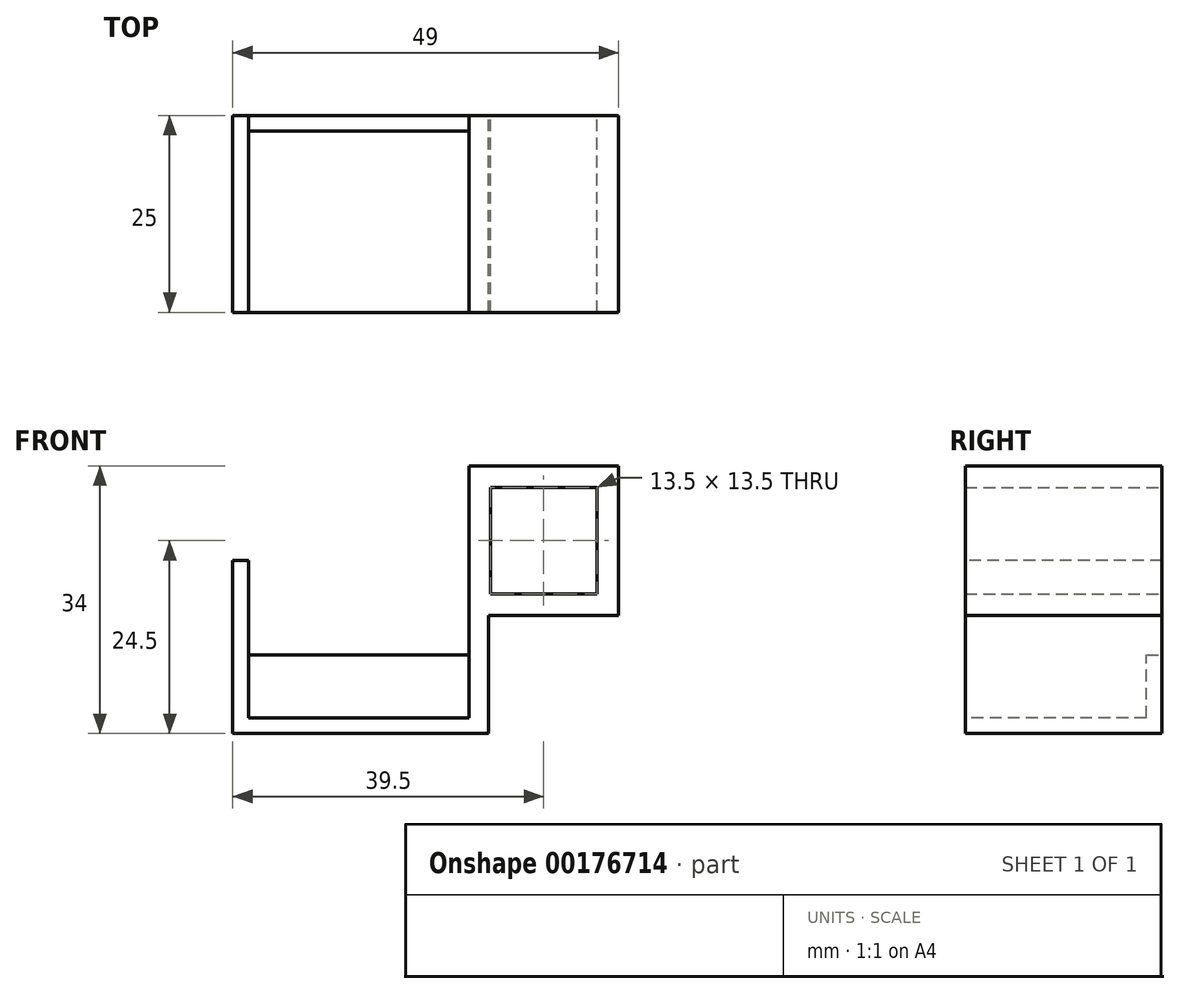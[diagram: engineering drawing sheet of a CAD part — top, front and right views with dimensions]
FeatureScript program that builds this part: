
annotation { "Feature Type Name" : "Feature", "Feature Type Description" : "" }
export const myFeature = defineFeature(function(context is Context, id is Id, definition is map)
    precondition{}
    {
        {
            var Q0;
            Q0=qCreatedBy(makeId("Front.planeOp"),FACE);
            var sketch = newSketch(context, id + "F0", { "sketchPlane" : qUnion([Q0])});
            skLineSegment(sketch, "E0.bottom", {"start": v(9.5, 9.5) * mm, "end": v(-9.5, 9.5) * mm});
            skLineSegment(sketch, "E0.top", {"start": v(9.5, -9.5) * mm, "end": v(-9.5, -9.5) * mm});
            skLineSegment(sketch, "E0.left", {"start": v(9.5, 9.5) * mm, "end": v(9.5, -9.5) * mm});
            skLineSegment(sketch, "E0.right", {"start": v(-9.5, 9.5) * mm, "end": v(-9.5, -9.5) * mm});
            skPoint(sketch, "E0.middle", {"position": v(0, 0) * mm});
            skLineSegment(sketch, "E1.bottom", {"start": v(6.75, 6.75) * mm, "end": v(-6.75, 6.75) * mm});
            skLineSegment(sketch, "E1.top", {"start": v(6.75, -6.75) * mm, "end": v(-6.75, -6.75) * mm});
            skLineSegment(sketch, "E1.left", {"start": v(6.75, 6.75) * mm, "end": v(6.75, -6.75) * mm});
            skLineSegment(sketch, "E1.right", {"start": v(-6.75, 6.75) * mm, "end": v(-6.75, -6.75) * mm});
            skSolve(sketch);
        }
        {
            var Q0;
            Q0=qSketchRegion(id+"F0",true);
            extrude(context, id + "F1", {"entities" : qUnion([Q0]), "endBound" : BoundingType.SYMMETRIC, "depth" : 25 * mm});
        }
        {
            var Q0;
            Q0=makeQuery(id+"F1.opExtrude","SWEPT_FACE",FACE,{"disambiguationData":[OSD([sQuery(id+"F0.wireOp",EDGE,"E0.right")])]});
            var sketch = newSketch(context, id + "F2", { "sketchPlane" : qUnion([Q0])});
            skLineSegment(sketch, "E2.bottom", {"start": v(-12.5, 9.5) * mm, "end": v(12.5, 9.5) * mm});
            skLineSegment(sketch, "E2.top", {"start": v(-12.5, -24.5) * mm, "end": v(12.5, -24.5) * mm});
            skLineSegment(sketch, "E2.left", {"start": v(-12.5, 9.5) * mm, "end": v(-12.5, -24.5) * mm});
            skLineSegment(sketch, "E2.right", {"start": v(12.5, 9.5) * mm, "end": v(12.5, -24.5) * mm});
            skSolve(sketch);
        }
        {
            var Q0;
            Q0=qSketchRegion(id+"F2",true);
            extrude(context, id + "F3", {"entities" : qUnion([Q0]), "operationType" : NewBodyOperationType.ADD, "oppositeDirection" : true, "depth" : 2.5 * mm});
        }
        {
            var Q0;
            Q0=makeQuery(id+"F3.boolean.opBoolean","MERGE",FACE,{"derivedFrom":[makeQuery(id+"F1.opExtrude","SWEPT_FACE",FACE,{"disambiguationData":[OSD([sQuery(id+"F0.wireOp",EDGE,"E0.right")])]}),makeQuery(id+"F3.opExtrude","CAP_FACE",FACE,{"disambiguationData":[OSD([sQuery(id+"F2.wireOp",EDGE,"E2.bottom"),sQuery(id+"F2.wireOp",EDGE,"E2.top"),sQuery(id+"F2.wireOp",EDGE,"E2.left"),sQuery(id+"F2.wireOp",EDGE,"E2.right")])],"isStart":true})]});
            var sketch = newSketch(context, id + "F4", { "sketchPlane" : qUnion([Q0])});
            skLineSegment(sketch, "E3.bottom", {"start": v(-12.5, -24.5) * mm, "end": v(12.5, -24.5) * mm});
            skLineSegment(sketch, "E3.top", {"start": v(-12.5, -22.5) * mm, "end": v(12.5, -22.5) * mm});
            skLineSegment(sketch, "E3.left", {"start": v(-12.5, -24.5) * mm, "end": v(-12.5, -22.5) * mm});
            skLineSegment(sketch, "E3.right", {"start": v(12.5, -24.5) * mm, "end": v(12.5, -22.5) * mm});
            skSolve(sketch);
        }
        {
            var Q0;
            Q0=qSketchRegion(id+"F4",true);
            extrude(context, id + "F5", {"entities" : qUnion([Q0]), "operationType" : NewBodyOperationType.ADD, "depth" : 30 * mm});
        }
        {
            var Q0;
            Q0=makeQuery(id+"F5.opExtrude","SWEPT_FACE",FACE,{"disambiguationData":[OSD([sQuery(id+"F4.wireOp",EDGE,"E3.top")])]});
            var sketch = newSketch(context, id + "F6", { "sketchPlane" : qUnion([Q0])});
            skLineSegment(sketch, "E4.bottom", {"start": v(-39.5, 12.5) * mm, "end": v(-37.5, 12.5) * mm});
            skLineSegment(sketch, "E4.top", {"start": v(-39.5, -12.5) * mm, "end": v(-37.5, -12.5) * mm});
            skLineSegment(sketch, "E4.left", {"start": v(-39.5, 12.5) * mm, "end": v(-39.5, -12.5) * mm});
            skLineSegment(sketch, "E4.right", {"start": v(-37.5, 12.5) * mm, "end": v(-37.5, -12.5) * mm});
            skSolve(sketch);
        }
        {
            var Q0;
            Q0=qSketchRegion(id+"F6",true);
            extrude(context, id + "F7", {"entities" : qUnion([Q0]), "operationType" : NewBodyOperationType.ADD, "depth" : 20 * mm});
        }
        {
            var Q0;
            Q0=makeQuery(id+"F7.boolean.opBoolean","MERGE",FACE,{"derivedFrom":[makeQuery(id+"F5.boolean.opBoolean","MERGE",FACE,{"derivedFrom":[makeQuery(id+"F3.boolean.opBoolean","MERGE",FACE,{"derivedFrom":[makeQuery(id+"F1.opExtrude","CAP_FACE",FACE,{"disambiguationData":[OSD([sQuery(id+"F0.wireOp",EDGE,"E0.bottom"),sQuery(id+"F0.wireOp",EDGE,"E0.top"),sQuery(id+"F0.wireOp",EDGE,"E0.left"),sQuery(id+"F0.wireOp",EDGE,"E0.right"),sQuery(id+"F0.wireOp",EDGE,"E1.bottom"),sQuery(id+"F0.wireOp",EDGE,"E1.top"),sQuery(id+"F0.wireOp",EDGE,"E1.left"),sQuery(id+"F0.wireOp",EDGE,"E1.right")])],"isStart":true}),makeQuery(id+"F3.opExtrude","SWEPT_FACE",FACE,{"disambiguationData":[OSD([sQuery(id+"F2.wireOp",EDGE,"E2.left")])]})]}),makeQuery(id+"F5.opExtrude","SWEPT_FACE",FACE,{"disambiguationData":[OSD([sQuery(id+"F4.wireOp",EDGE,"E3.left")])]})]}),makeQuery(id+"F7.opExtrude","SWEPT_FACE",FACE,{"disambiguationData":[OSD([sQuery(id+"F6.wireOp",EDGE,"E4.bottom")])]})]});
            var sketch = newSketch(context, id + "F8", { "sketchPlane" : qUnion([Q0])});
            skLineSegment(sketch, "E5.bottom", {"start": v(7, -24.5) * mm, "end": v(39.5, -24.5) * mm});
            skLineSegment(sketch, "E5.top", {"start": v(7, -14.5) * mm, "end": v(39.5, -14.5) * mm});
            skLineSegment(sketch, "E5.left", {"start": v(7, -24.5) * mm, "end": v(7, -14.5) * mm});
            skLineSegment(sketch, "E5.right", {"start": v(39.5, -24.5) * mm, "end": v(39.5, -14.5) * mm});
            skSolve(sketch);
        }
        {
            var Q0;
            Q0 = qSketchRegion(id + "F8", true);
            extrude(context, id + "F9", {"entities" : qUnion([Q0]), "operationType" : NewBodyOperationType.ADD, "oppositeDirection" : true, "depth" : 2 * mm});
        }
    });
